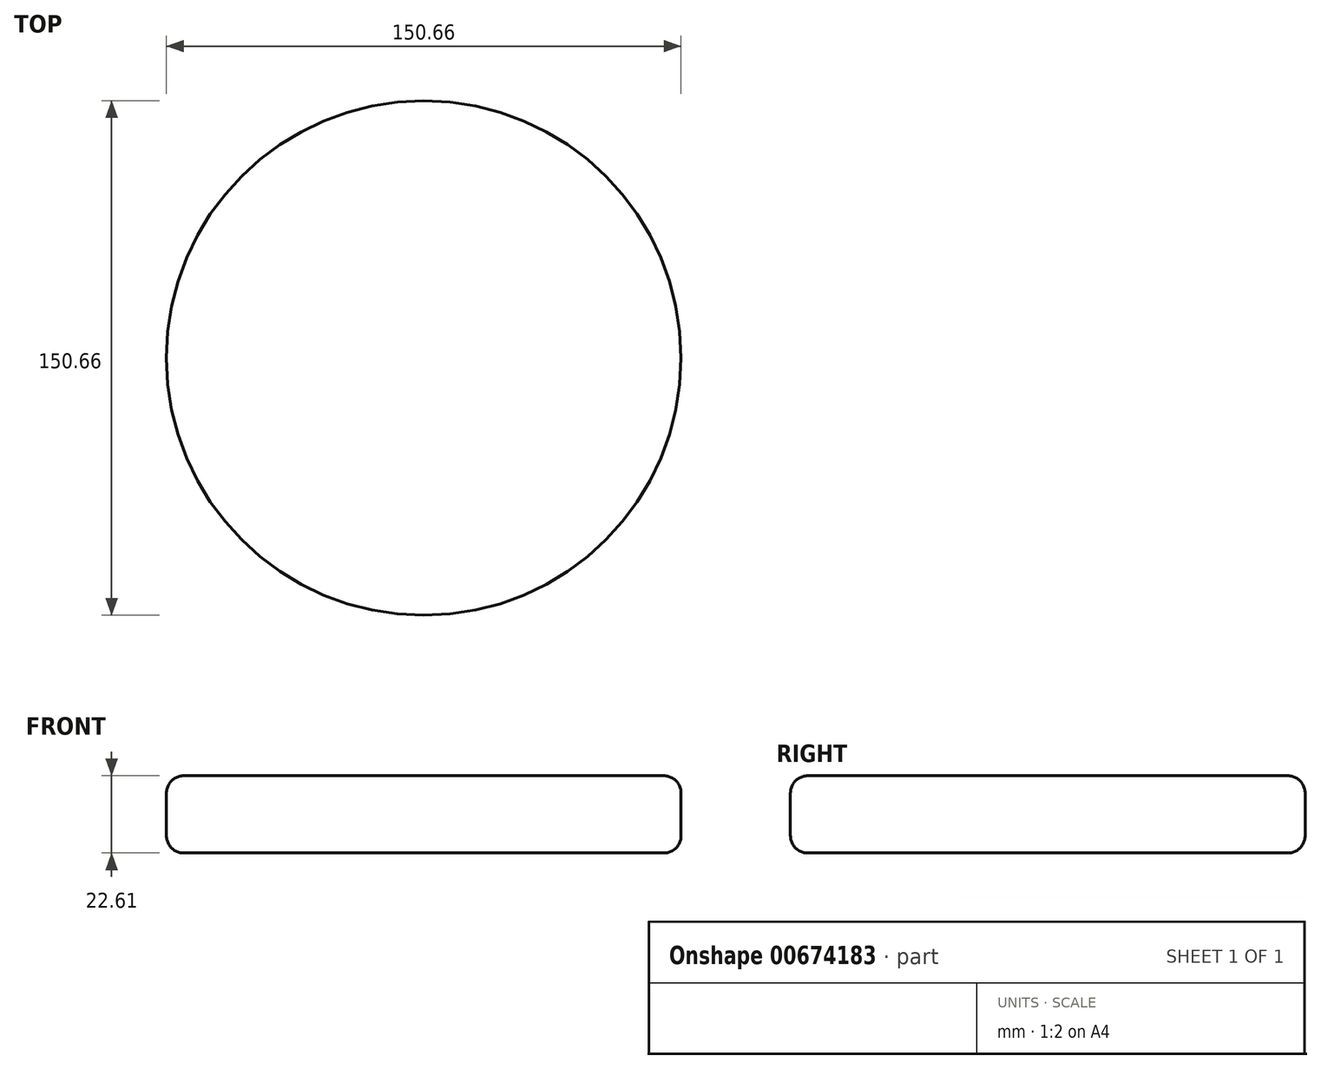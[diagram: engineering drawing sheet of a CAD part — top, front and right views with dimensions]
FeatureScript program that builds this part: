
annotation { "Feature Type Name" : "Feature", "Feature Type Description" : "" }
export const myFeature = defineFeature(function(context is Context, id is Id, definition is map)
    precondition{}
    {
        {
            var Q0;
            Q0=qCreatedBy(makeId("Top.planeOp"),FACE);
            var sketch = newSketch(context, id + "F0", { "sketchPlane" : qUnion([Q0])});
            skCircle(sketch, "E0", {"center": v(0, 0) * mm, "radius": 75.33 * mm});
            skSolve(sketch);
        }
        {
            var Q0;
            Q0=makeQuery(id+"F0.imprint","IMPRINT",FACE,{"disambiguationData":[TD([[makeQuery(id+"F0.imprint","IMPRINT",EDGE,{"derivedFrom":sQuery(id+"F0.wireOp",EDGE,"E0")}),1.0]])]});
            extrude(context, id + "F1", {"entities" : qUnion([Q0]), "depth" : 22.6 * mm, "offsetDistance" : 25.4 * mm});
        }
        {
            var Q0;
            Q0=makeQuery(id+"F1.opExtrude","CAP_EDGE",EDGE,{"disambiguationData":[OSD([sQuery(id+"F0.wireOp",EDGE,"E0")])],"isStart":true});
            fillet(context, id + "F2", {"entities" : qUnion([Q0]), "radius" : 5.08 * mm, "tangentPropagation" : true, "allowEdgeOverflow" : false});
        }
        {
            var Q0;
            Q0=makeQuery(id+"F1.opExtrude","SWEPT_FACE",FACE,{"disambiguationData":[OSD([sQuery(id+"F0.wireOp",EDGE,"E0")])]});
            var Q1;
            {var subQ0=sQuery(id+"F0.wireOp",EDGE,"E0");Q1=makeQuery(id+"FteNCINpc0hQt57_1.opFillet","BLEND_EDGE",EDGE,{"blendedFrom":[makeQuery(id+"F1.opExtrude","CAP_EDGE",EDGE,{"disambiguationData":[OSD([subQ0])],"isStart":false}),makeQuery(id+"F1.opExtrude","SWEPT_FACE",FACE,{"disambiguationData":[OSD([subQ0])]})],"blendedInto":[makeQuery(id+"F1.opExtrude","SWEPT_FACE",FACE,{"disambiguationData":[OSD([subQ0])]})]});}
            fillet(context, id + "F3", {"entities" : qUnion([Q0, Q1]), "radius" : 5.08 * mm, "tangentPropagation" : true, "allowEdgeOverflow" : false});
        }
    });
